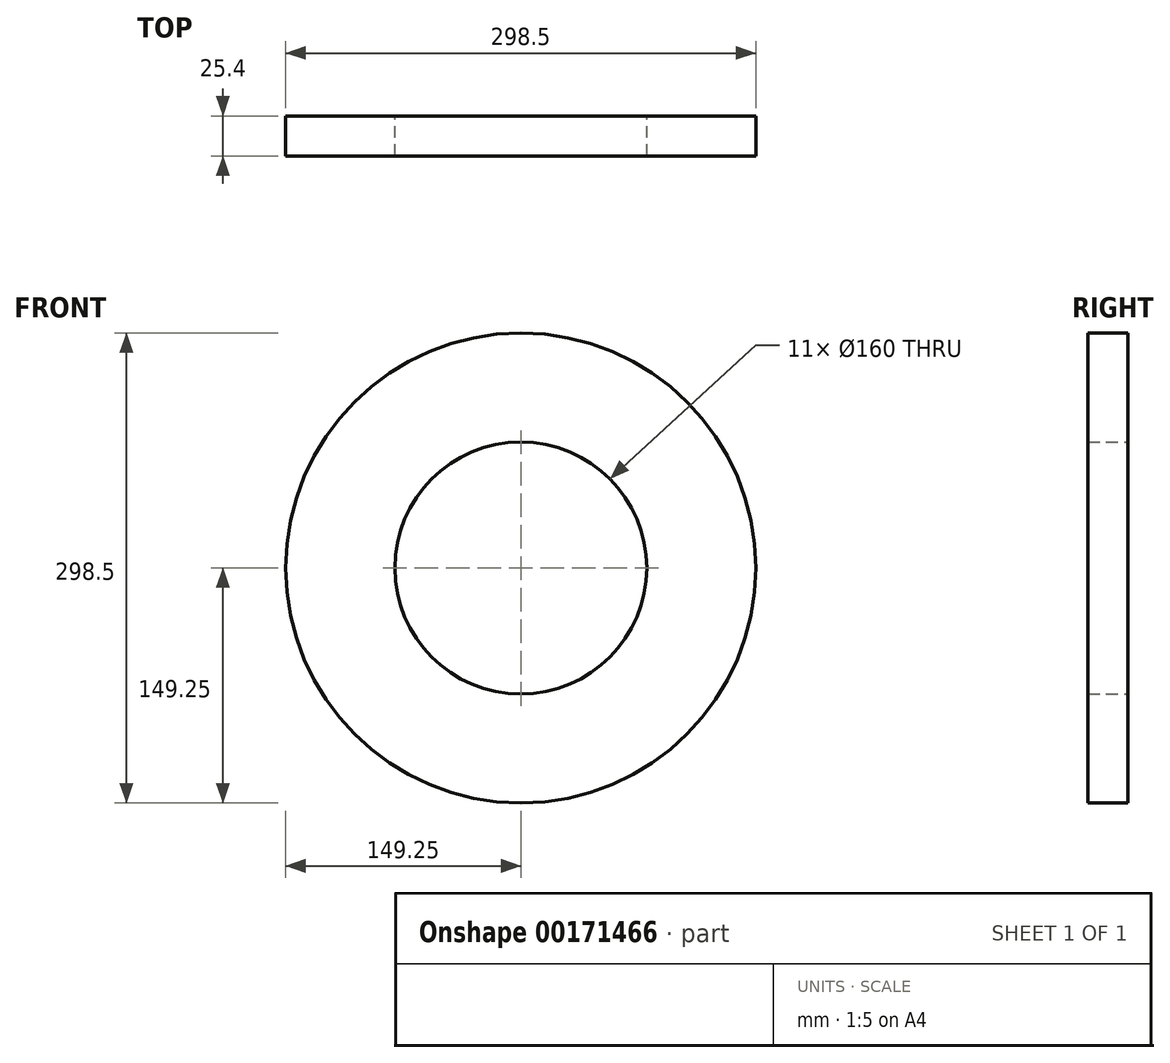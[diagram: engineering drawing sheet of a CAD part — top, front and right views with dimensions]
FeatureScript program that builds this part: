
annotation { "Feature Type Name" : "Feature", "Feature Type Description" : "" }
export const myFeature = defineFeature(function(context is Context, id is Id, definition is map)
    precondition{}
    {
        {
            var Q0;
            Q0=qCreatedBy(makeId("Front.planeOp"),FACE);
            var sketch = newSketch(context, id + "F0", { "sketchPlane" : qUnion([Q0])});
            skCircle(sketch, "E0", {"center": v(0, 0) * mm, "radius": 149.25 * mm});
            skCircle(sketch, "E1", {"center": v(0, 0) * mm, "radius": 80 * mm});
            skSolve(sketch);
        }
        {
            var Q0;
            Q0 = qSketchRegion(id + "F0", true);
            extrude(context, id + "F1", {"entities" : qUnion([Q0]), "depth" : 25.4 * mm});
        }
    });
